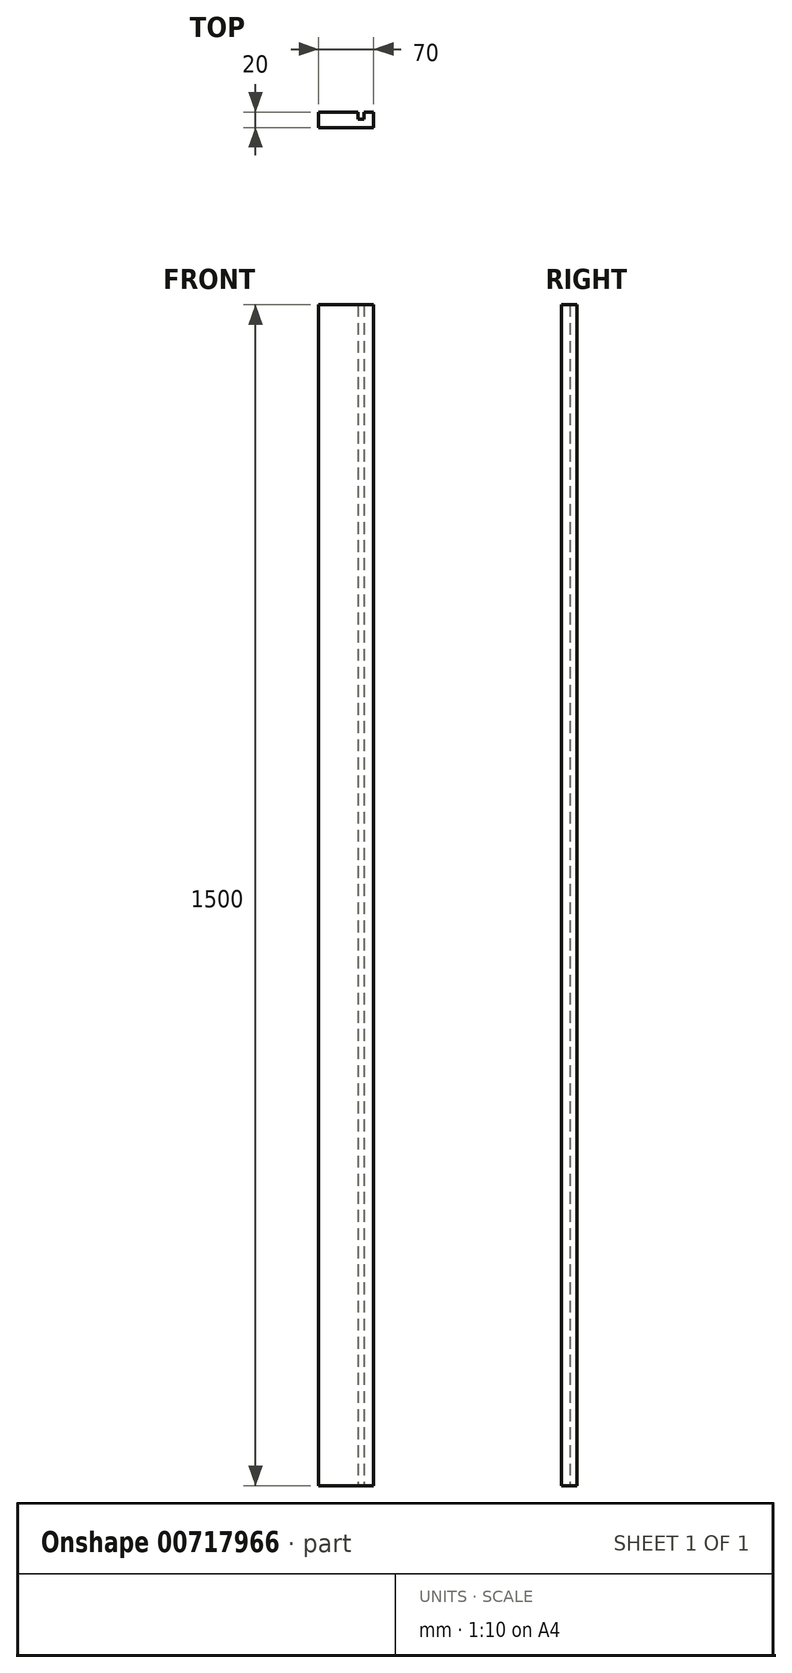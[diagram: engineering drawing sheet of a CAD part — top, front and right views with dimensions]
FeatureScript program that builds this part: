
annotation { "Feature Type Name" : "Feature", "Feature Type Description" : "" }
export const myFeature = defineFeature(function(context is Context, id is Id, definition is map)
    precondition{}
    {
        {
            var Q0;
            Q0=qCreatedBy(makeId("Front.planeOp"),FACE);
            var sketch = newSketch(context, id + "F0", { "sketchPlane" : qUnion([Q0])});
            skLineSegment(sketch, "E0.bottom", {"start": v(-93.13, 1274.72) * mm, "end": v(-23.13, 1274.72) * mm});
            skLineSegment(sketch, "E0.top", {"start": v(-93.13, -225.28) * mm, "end": v(-23.13, -225.28) * mm});
            skLineSegment(sketch, "E0.left", {"start": v(-93.13, 1274.72) * mm, "end": v(-93.13, -225.28) * mm});
            skLineSegment(sketch, "E0.right", {"start": v(-23.13, 1274.72) * mm, "end": v(-23.13, -225.28) * mm});
            skSolve(sketch);
        }
        {
            var Q0;
            Q0 = qSketchRegion(id + "F0", true);
            extrude(context, id + "F1", {"entities" : qUnion([Q0]), "oppositeDirection" : true, "depth" : 20 * mm, "offsetDistance" : 25.4 * mm});
        }
        {
            var Q0;
            Q0=makeQuery(id+"F1.opExtrude","CAP_FACE",FACE,{"disambiguationData":[OSD([sQuery(id+"F0.wireOp",EDGE,"E0.bottom"),sQuery(id+"F0.wireOp",EDGE,"E0.top"),sQuery(id+"F0.wireOp",EDGE,"E0.left"),sQuery(id+"F0.wireOp",EDGE,"E0.right")])],"isStart":false});
            var sketch = newSketch(context, id + "F2", { "sketchPlane" : qUnion([Q0])});
            skLineSegment(sketch, "E1.bottom", {"start": v(35.13, 1274.72) * mm, "end": v(43.13, 1274.72) * mm});
            skLineSegment(sketch, "E1.top", {"start": v(35.13, -225.28) * mm, "end": v(43.13, -225.28) * mm});
            skLineSegment(sketch, "E1.left", {"start": v(35.13, 1274.72) * mm, "end": v(35.13, -225.28) * mm});
            skLineSegment(sketch, "E1.right", {"start": v(43.13, 1274.72) * mm, "end": v(43.13, -225.28) * mm});
            skSolve(sketch);
        }
        {
            var Q0;
            Q0=makeQuery(id+"F2.imprint","IMPRINT",FACE,{"disambiguationData":[TD([[makeQuery(id+"F2.imprint","IMPRINT",EDGE,{"derivedFrom":sQuery(id+"F2.wireOp",EDGE,"E1.bottom")}),1.0]])]});
            extrude(context, id + "F3", {"entities" : qUnion([Q0]), "operationType" : NewBodyOperationType.REMOVE, "oppositeDirection" : true, "depth" : 9 * mm, "offsetDistance" : 25.4 * mm});
        }
    });
